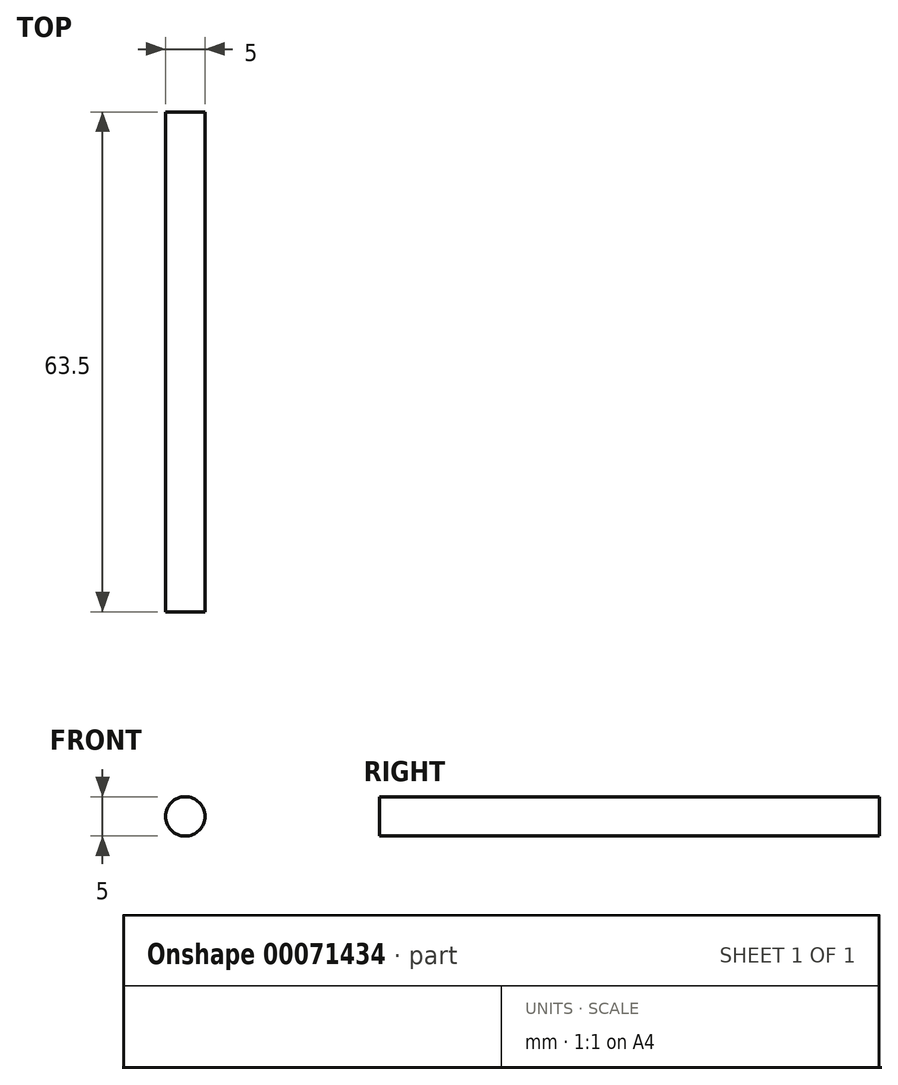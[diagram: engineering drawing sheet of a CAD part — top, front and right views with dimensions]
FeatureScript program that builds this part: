
annotation { "Feature Type Name" : "Feature", "Feature Type Description" : "" }
export const myFeature = defineFeature(function(context is Context, id is Id, definition is map)
    precondition{}
    {
        {
            var Q0;
            Q0=qCreatedBy(makeId("Front.planeOp"),FACE);
            var sketch = newSketch(context, id + "F0", { "sketchPlane" : qUnion([Q0])});
            skCircle(sketch, "E0", {"center": v(0, 0) * mm, "radius": 2.5 * mm});
            skSolve(sketch);
        }
        {
            var Q0;
            Q0=makeQuery(id+"F0.imprint","IMPRINT",FACE,{"disambiguationData":[TD([[makeQuery(id+"F0.imprint","IMPRINT",EDGE,{"derivedFrom":sQuery(id+"F0.wireOp",EDGE,"E0")}),1.0]])]});
            extrude(context, id + "F1", {"entities" : qUnion([Q0]), "depth" : 63.5 * mm});
        }
    });
